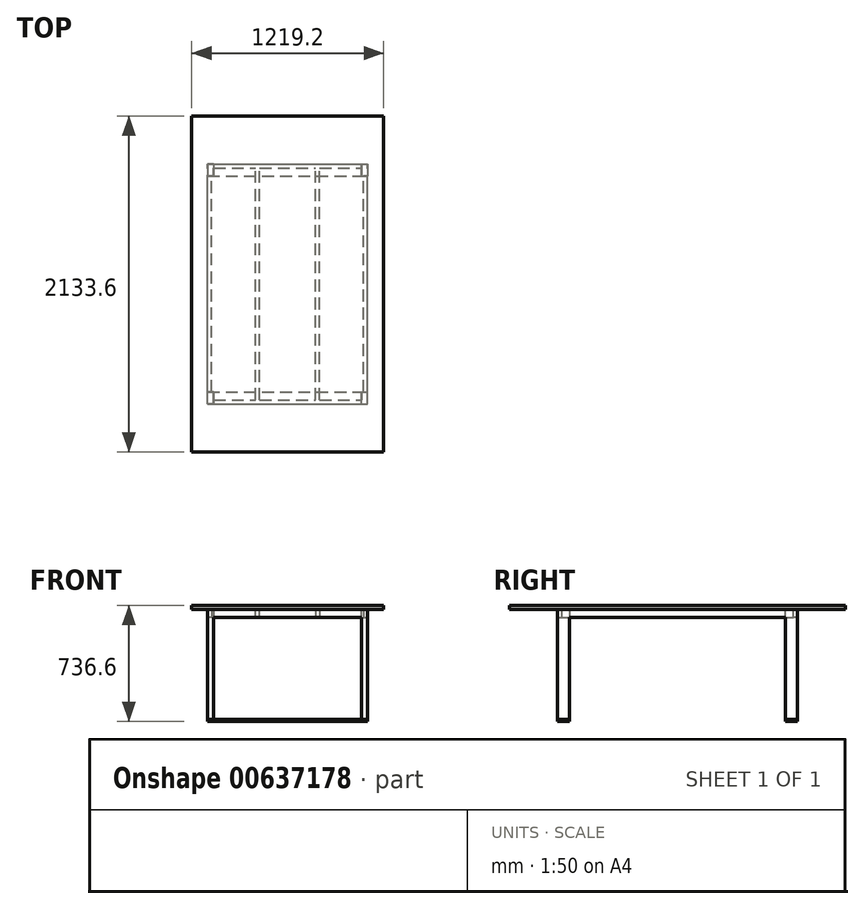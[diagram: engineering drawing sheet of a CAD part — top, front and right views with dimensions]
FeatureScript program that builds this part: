
annotation { "Feature Type Name" : "Feature", "Feature Type Description" : "" }
export const myFeature = defineFeature(function(context is Context, id is Id, definition is map)
    precondition{}
    {
        {
            var Q0;
            Q0=qCreatedBy(makeId("Top.planeOp"),FACE);
            var sketch = newSketch(context, id + "F0", { "sketchPlane" : qUnion([Q0])});
            skLineSegment(sketch, "E0.bottom", {"start": v(-609.6, 1066.8) * mm, "end": v(609.6, 1066.8) * mm});
            skLineSegment(sketch, "E0.top", {"start": v(-609.6, -1066.8) * mm, "end": v(609.6, -1066.8) * mm});
            skLineSegment(sketch, "E0.left", {"start": v(-609.6, 1066.8) * mm, "end": v(-609.6, -1066.8) * mm});
            skLineSegment(sketch, "E0.right", {"start": v(609.6, 1066.8) * mm, "end": v(609.6, -1066.8) * mm});
            skSolve(sketch);
        }
        {
            var Q0;
            Q0=makeQuery(id+"F0.imprint","IMPRINT",FACE,{"disambiguationData":[TD([[makeQuery(id+"F0.imprint","IMPRINT",EDGE,{"derivedFrom":sQuery(id+"F0.wireOp",EDGE,"E0.bottom")}),-1.0]])]});
            var Q1;
            Q1 = qSketchRegion(id + "F2", true);
            extrude(context, id + "F1", {"entities" : qUnion([Q0, Q1]), "depth" : 25.4 * mm, "offsetDistance" : 25.4 * mm});
        }
        {
            var Q0;
            Q0=makeQuery(id+"F0.imprint","IMPRINT",FACE,{"disambiguationData":[TD([[makeQuery(id+"F0.imprint","IMPRINT",EDGE,{"derivedFrom":sQuery(id+"F0.wireOp",EDGE,"E0.bottom")}),-1.0]])]});
            var sketch = newSketch(context, id + "F2", { "sketchPlane" : qUnion([Q0])});
            skLineSegment(sketch, "E1.bottom", {"start": v(508, -762) * mm, "end": v(482.6, -762) * mm});
            skLineSegment(sketch, "E1.top", {"start": v(508, 762) * mm, "end": v(482.6, 762) * mm});
            skLineSegment(sketch, "E1.left", {"start": v(508, -762) * mm, "end": v(508, 762) * mm});
            skLineSegment(sketch, "E1.right", {"start": v(482.6, -762) * mm, "end": v(482.6, 762) * mm});
            skSolve(sketch);
        }
        {
            var Q0;
            Q0 = qSketchRegion(id + "F2", true);
            extrude(context, id + "F3", {"entities" : qUnion([Q0]), "depth" : -50.8 * mm, "offsetDistance" : 25.4 * mm});
        }
        {
            var Q0;
            Q0=makeQuery(id+"F3.opExtrude","SWEPT_BODY",BODY,{"disambiguationData":[OSD([sQuery(id+"F2.wireOp",EDGE,"E1.bottom"),sQuery(id+"F2.wireOp",EDGE,"E1.top"),sQuery(id+"F2.wireOp",EDGE,"E1.left"),sQuery(id+"F2.wireOp",EDGE,"E1.right")])]});
            var Q1;
            Q1=qCreatedBy(makeId("Right.planeOp"),FACE);
            mirror(context, id + "F4", {"entities" : qUnion([Q0]), "mirrorPlane" : qUnion([Q1])});
        }
        {
            var Q0;
            Q0=makeQuery(id+"F0.imprint","IMPRINT",FACE,{"disambiguationData":[TD([[makeQuery(id+"F0.imprint","IMPRINT",EDGE,{"derivedFrom":sQuery(id+"F0.wireOp",EDGE,"E0.bottom")}),-1.0]])]});
            var sketch = newSketch(context, id + "F5", { "sketchPlane" : qUnion([Q0])});
            skLineSegment(sketch, "E2.bottom", {"start": v(-508, -762) * mm, "end": v(508, -762) * mm});
            skLineSegment(sketch, "E2.top", {"start": v(-508, -736.6) * mm, "end": v(508, -736.6) * mm});
            skLineSegment(sketch, "E2.left", {"start": v(-508, -762) * mm, "end": v(-508, -736.6) * mm});
            skLineSegment(sketch, "E2.right", {"start": v(508, -762) * mm, "end": v(508, -736.6) * mm});
            skSolve(sketch);
        }
        {
            var Q0;
            Q0 = qSketchRegion(id + "F5", true);
            extrude(context, id + "F6", {"entities" : qUnion([Q0]), "depth" : -50.8 * mm, "offsetDistance" : 25.4 * mm});
        }
        {
            var Q0;
            Q0=makeQuery(id+"F6.opExtrude","SWEPT_BODY",BODY,{"disambiguationData":[OSD([sQuery(id+"F5.wireOp",EDGE,"E2.bottom"),sQuery(id+"F5.wireOp",EDGE,"E2.top"),sQuery(id+"F5.wireOp",EDGE,"E2.left"),sQuery(id+"F5.wireOp",EDGE,"E2.right")])]});
            var Q1;
            Q1=qCreatedBy(makeId("Front.planeOp"),FACE);
            mirror(context, id + "F7", {"entities" : qUnion([Q0]), "mirrorPlane" : qUnion([Q1])});
        }
        {
            var Q0;
            Q0=makeQuery(id+"F4.opPattern","COPY",FACE,{"derivedFrom":makeQuery(id+"F3.opExtrude","SWEPT_FACE",FACE,{"disambiguationData":[OSD([sQuery(id+"F2.wireOp",EDGE,"E1.left")])]}),"instanceName":"1"});
            var sketch = newSketch(context, id + "F8", { "sketchPlane" : qUnion([Q0])});
            skLineSegment(sketch, "E3.bottom", {"start": v(-762, 0) * mm, "end": v(-685.8, 0) * mm});
            skLineSegment(sketch, "E3.top", {"start": v(-762, -711.2) * mm, "end": v(-685.8, -711.2) * mm});
            skLineSegment(sketch, "E3.left", {"start": v(-762, 0) * mm, "end": v(-762, -711.2) * mm});
            skLineSegment(sketch, "E3.right", {"start": v(-685.8, 0) * mm, "end": v(-685.8, -711.2) * mm});
            skSolve(sketch);
        }
        {
            var Q0;
            Q0 = qSketchRegion(id + "F8", true);
            extrude(context, id + "F9", {"entities" : qUnion([Q0]), "depth" : -38.1 * mm, "offsetDistance" : 25.4 * mm});
        }
        {
            var Q0;
            Q0=makeQuery(id+"F9.opExtrude","SWEPT_BODY",BODY,{"disambiguationData":[OSD([sQuery(id+"F8.wireOp",EDGE,"E3.bottom"),sQuery(id+"F8.wireOp",EDGE,"E3.top"),sQuery(id+"F8.wireOp",EDGE,"E3.left"),sQuery(id+"F8.wireOp",EDGE,"E3.right")])]});
            var Q1;
            Q1=qCreatedBy(makeId("Right.planeOp"),FACE);
            mirror(context, id + "F10", {"entities" : qUnion([Q0]), "mirrorPlane" : qUnion([Q1])});
        }
        {
            var Q0;
            Q0=makeQuery(id+"F10.opPattern","COPY",BODY,{"derivedFrom":makeQuery(id+"F9.opExtrude","SWEPT_BODY",BODY,{"disambiguationData":[OSD([sQuery(id+"F8.wireOp",EDGE,"E3.bottom"),sQuery(id+"F8.wireOp",EDGE,"E3.top"),sQuery(id+"F8.wireOp",EDGE,"E3.left"),sQuery(id+"F8.wireOp",EDGE,"E3.right")])]}),"instanceName":"1"});
            var Q1;
            Q1=makeQuery(id+"F9.opExtrude","SWEPT_BODY",BODY,{"disambiguationData":[OSD([sQuery(id+"F8.wireOp",EDGE,"E3.bottom"),sQuery(id+"F8.wireOp",EDGE,"E3.top"),sQuery(id+"F8.wireOp",EDGE,"E3.left"),sQuery(id+"F8.wireOp",EDGE,"E3.right")])]});
            var Q2;
            Q2=qCreatedBy(makeId("Front.planeOp"),FACE);
            mirror(context, id + "F11", {"operationType" : NewBodyOperationType.ADD, "entities" : qUnion([Q0, Q1]), "mirrorPlane" : qUnion([Q2])});
        }
        {
            var Q0;
            Q0=makeQuery(id+"F11.opPattern","COPY",FACE,{"derivedFrom":makeQuery(id+"F9.opExtrude","SWEPT_FACE",FACE,{"disambiguationData":[OSD([sQuery(id+"F8.wireOp",EDGE,"E3.top")])]}),"instanceName":"1"});
            var sketch = newSketch(context, id + "F12", { "sketchPlane" : qUnion([Q0])});
            skLineSegment(sketch, "E4.bottom", {"start": v(-508, 762) * mm, "end": v(508, 762) * mm});
            skLineSegment(sketch, "E4.top", {"start": v(-508, 685.8) * mm, "end": v(508, 685.8) * mm});
            skLineSegment(sketch, "E4.left", {"start": v(-508, 762) * mm, "end": v(-508, 685.8) * mm});
            skLineSegment(sketch, "E4.right", {"start": v(508, 762) * mm, "end": v(508, 685.8) * mm});
            skSolve(sketch);
        }
        {
            var Q0;
            Q0 = qSketchRegion(id + "F12", true);
            extrude(context, id + "F13", {"entities" : qUnion([Q0]), "depth" : -12.7 * mm, "offsetDistance" : 25.4 * mm});
        }
        {
            var Q0;
            Q0=makeQuery(id+"F13.opExtrude","SWEPT_BODY",BODY,{"disambiguationData":[OSD([sQuery(id+"F12.wireOp",EDGE,"E4.bottom"),sQuery(id+"F12.wireOp",EDGE,"E4.top"),sQuery(id+"F12.wireOp",EDGE,"E4.left"),sQuery(id+"F12.wireOp",EDGE,"E4.right")])]});
            var Q1;
            Q1=qCreatedBy(makeId("Front.planeOp"),FACE);
            mirror(context, id + "F14", {"entities" : qUnion([Q0]), "mirrorPlane" : qUnion([Q1])});
        }
        {
            var Q0;
            Q0=makeQuery(id+"F0.imprint","IMPRINT",FACE,{"disambiguationData":[TD([[makeQuery(id+"F0.imprint","IMPRINT",EDGE,{"derivedFrom":sQuery(id+"F0.wireOp",EDGE,"E0.bottom")}),-1.0]])]});
            var sketch = newSketch(context, id + "F15", { "sketchPlane" : qUnion([Q0])});
            skLineSegment(sketch, "E5.bottom", {"start": v(-203.2, -762) * mm, "end": v(-177.8, -762) * mm});
            skLineSegment(sketch, "E5.top", {"start": v(-203.2, 762) * mm, "end": v(-177.8, 762) * mm});
            skLineSegment(sketch, "E5.left", {"start": v(-203.2, -762) * mm, "end": v(-203.2, 762) * mm});
            skLineSegment(sketch, "E5.right", {"start": v(-177.8, -762) * mm, "end": v(-177.8, 762) * mm});
            skSolve(sketch);
        }
        {
            var Q0;
            Q0 = qSketchRegion(id + "F15", true);
            extrude(context, id + "F16", {"entities" : qUnion([Q0]), "depth" : -50.8 * mm, "offsetDistance" : 25.4 * mm});
        }
        {
            var Q0;
            Q0=makeQuery(id+"F16.opExtrude","SWEPT_BODY",BODY,{"disambiguationData":[OSD([sQuery(id+"F15.wireOp",EDGE,"E5.bottom"),sQuery(id+"F15.wireOp",EDGE,"E5.top"),sQuery(id+"F15.wireOp",EDGE,"E5.left"),sQuery(id+"F15.wireOp",EDGE,"E5.right")])]});
            var Q1;
            Q1=qCreatedBy(makeId("Right.planeOp"),FACE);
            mirror(context, id + "F17", {"operationType" : NewBodyOperationType.ADD, "entities" : qUnion([Q0]), "mirrorPlane" : qUnion([Q1])});
        }
    });
